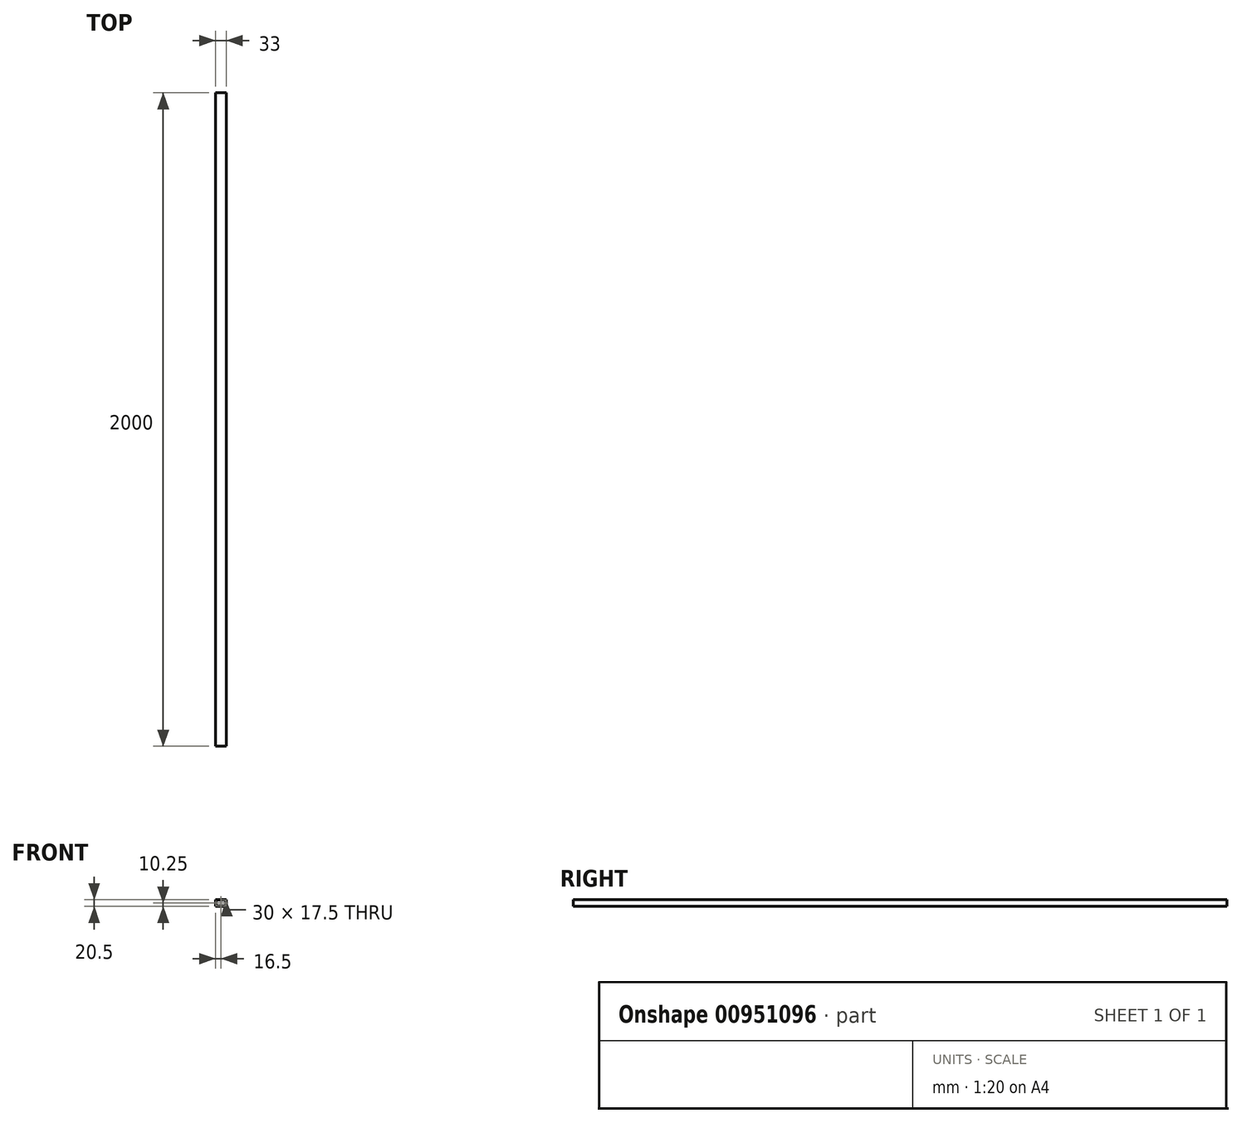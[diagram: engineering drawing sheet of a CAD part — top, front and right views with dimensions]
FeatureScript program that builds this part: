
annotation { "Feature Type Name" : "Feature", "Feature Type Description" : "" }
export const myFeature = defineFeature(function(context is Context, id is Id, definition is map)
    precondition{}
    {
        {
            var Q0;
            Q0=qCreatedBy(makeId("Front.planeOp"),FACE);
            var sketch = newSketch(context, id + "F0", { "sketchPlane" : qUnion([Q0])});
            skLineSegment(sketch, "E0.bottom", {"start": v(0, 0) * mm, "end": v(33, 0) * mm});
            skLineSegment(sketch, "E0.top", {"start": v(0, 20.5) * mm, "end": v(33, 20.5) * mm});
            skLineSegment(sketch, "E0.left", {"start": v(0, 0) * mm, "end": v(0, 20.5) * mm});
            skLineSegment(sketch, "E0.right", {"start": v(33, 0) * mm, "end": v(33, 20.5) * mm});
            skLineSegment(sketch, "E1.0", {"start": v(1.5, 1.5) * mm, "end": v(1.5, 19) * mm});
            skLineSegment(sketch, "E1.1", {"start": v(1.5, 1.5) * mm, "end": v(31.5, 1.5) * mm});
            skLineSegment(sketch, "E1.2", {"start": v(31.5, 1.5) * mm, "end": v(31.5, 19) * mm});
            skLineSegment(sketch, "E1.3", {"start": v(1.5, 19) * mm, "end": v(31.5, 19) * mm});
            skSolve(sketch);
        }
        {
            var Q0;
            Q0=makeQuery(id+"F0.imprint","IMPRINT",FACE,{"disambiguationData":[TD([[makeQuery(id+"F0.imprint","IMPRINT",EDGE,{"derivedFrom":sQuery(id+"F0.wireOp",EDGE,"E0.bottom")}),1.0]])]});
            extrude(context, id + "F1", {"entities" : qUnion([Q0]), "depth" : 2000 * mm, "offsetDistance" : 25 * mm});
        }
    });
